# Revit family: Domotics-DomesticRanges-GEWISS-SYSTEM_POWER-SOCKET-OUTLET_ITA_2xP11P17_16A
name_source: partatom
category: Apparecchi elettrici
revit_build: Autodesk Revit 2016 (Build: 20161004_0715(x64)
units: mm (PartAtom-declared; Revit-internal decimal feet)

## family parameters
Condiviso = Sì
Host = Superficie
Mantenere orientamento annotazione = Sì
Numero OmniClass = 23.80.50.14
Punto di calcolo locali = Sì
Quota connettore circolare = Usa diametro
Taglio con vuoti quando caricato = No
Tipo di parte = Normale
Titolo OmniClass = Plug Connectors

## types (2) — shared parameters
Carico apparente = 0 VA
Catalogue = DOMOTICS
Catalogue Range = SYSTEM - DOMESTIC RANGE
Description. = Double socket-outlet
Description: = 2x2P+E 16A Dual amp.
Electrocod = 0131
For plug pins = Ã˜ 4 / 5 mm
IDF = 791b834f-78d6-424e-986f-d4341bfbd1d3
IDT = d63e0260-b3b3-4258-9e79-1905bcf6cbcd
Immagine tipo = GW20291.jpg
Input = 1x16 A
Larghezza presa = 46 mm  [stored 0.150919 ft]
N. poli = 2
No. SYSTEM modules = 2
Produttore = GEWISS S.p.A.
Prospetto di default = 1219 mm
SEO = Socket outlet
Simbolo_ = SIMBOLO PRESE DOPPIE : PRESA DOPPIA
Standard = English
Standard: = English
Technical sheet = https://www.gewiss.com
Tipo_ = SYSTEM-PRESA-ITA-P11-17X2-16A_BASE : GW21291 - Nero - Presa multipla std italiano
Type = P17-11
URL = https://www.gewiss.com
Version file RFA = 19.4
Volt = 230 V
Voltage = 250 V ac
Voltage: = 250 V ac

## per-type parameters (varying)
| type | Colour | Descrizione | EAN code | Modello |
| GW20291 - 2P+E 16A ital.std double s.-outlet white | White | 2P+E 16A ITAL.STD DOUBLE S.-OUTLET SY/WT | 8011564054721 | GW20291 |
| GW21291 - 2P+E 16A ital.std double s.-outlet black | Black | 2P+E 16A ITAL.STD DOUBLE S.-OUTLET SY/BK | 8011564128439 | GW21291 |

note: [stored X ft] marks values corroborated as IEEE doubles in the binary element streams (Revit-internal decimal feet)

## geometry (parser evidence)
native form markers: Sweep x3
no freeform markers — native parametric forms only
